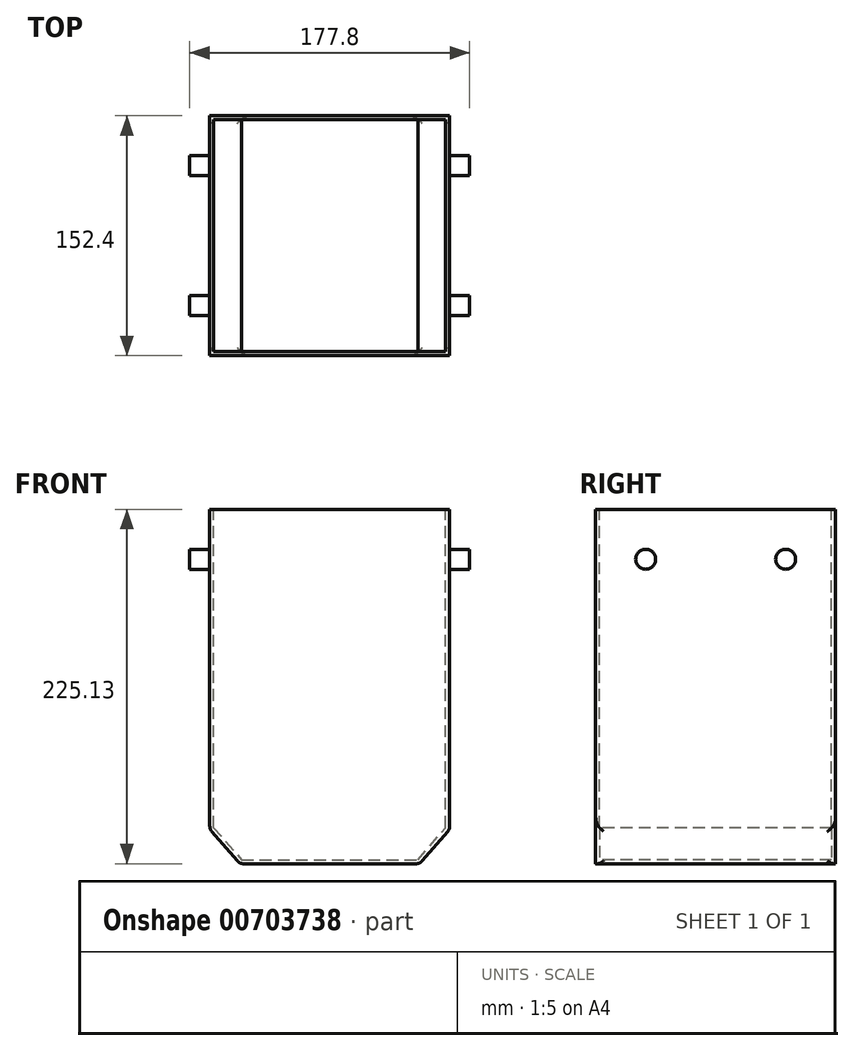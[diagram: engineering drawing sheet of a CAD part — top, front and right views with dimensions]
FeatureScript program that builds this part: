
annotation { "Feature Type Name" : "Feature", "Feature Type Description" : "" }
export const myFeature = defineFeature(function(context is Context, id is Id, definition is map)
    precondition{}
    {
        {
            var Q0;
            Q0=qCreatedBy(makeId("Front.planeOp"),FACE);
            var sketch = newSketch(context, id + "F0", { "sketchPlane" : qUnion([Q0])});
            skLineSegment(sketch, "E0.bottom", {"start": v(-76.2, -101.6) * mm, "end": v(76.2, -101.6) * mm});
            skLineSegment(sketch, "E0.top", {"start": v(-76.2, 101.6) * mm, "end": v(76.2, 101.6) * mm});
            skLineSegment(sketch, "E0.left", {"start": v(-76.2, -101.6) * mm, "end": v(-76.2, 101.6) * mm});
            skLineSegment(sketch, "E0.right", {"start": v(76.2, -101.6) * mm, "end": v(76.2, 101.6) * mm});
            skPoint(sketch, "E0.middle", {"position": v(0, 0) * mm});
            skLineSegment(sketch, "E1.bottom", {"start": v(-57.15, -123.53) * mm, "end": v(57.15, -123.53) * mm});
            skLineSegment(sketch, "E1.top", {"start": v(-57.15, -79.67) * mm, "end": v(57.15, -79.67) * mm});
            skLineSegment(sketch, "E1.left", {"start": v(-57.15, -123.53) * mm, "end": v(-57.15, -79.67) * mm});
            skLineSegment(sketch, "E1.right", {"start": v(57.15, -123.53) * mm, "end": v(57.15, -79.67) * mm});
            skPoint(sketch, "E1.middle", {"position": v(0, -101.6) * mm});
            skLineSegment(sketch, "E2", {"start": v(-76.2, -101.6) * mm, "end": v(-57.15, -123.53) * mm});
            skLineSegment(sketch, "E3", {"start": v(57.15, -123.53) * mm, "end": v(76.2, -101.6) * mm});
            skSolve(sketch);
        }
        {
            var Q0;
            {var subQ0=sQuery(id+"F0.wireOp",EDGE,"E2");Q0=makeQuery(id+"F0.imprint","IMPRINT",FACE,{"disambiguationData":[TD([[makeQuery(id+"F0.imprint","IMPRINT",EDGE,{"derivedFrom":subQ0}),1.0]])]});}
            var Q1;
            {var subQ0=sQuery(id+"F0.wireOp",EDGE,"E3");Q1=makeQuery(id+"F0.imprint","IMPRINT",FACE,{"disambiguationData":[TD([[makeQuery(id+"F0.imprint","IMPRINT",EDGE,{"derivedFrom":subQ0}),1.0]])]});}
            var Q2;
            Q2=makeQuery(id+"F0.imprint","IMPRINT",FACE,{"disambiguationData":[TD([[makeQuery(id+"F0.imprint","IMPRINT",EDGE,{"derivedFrom":sQuery(id+"F0.wireOp",EDGE,"E0.top")}),-1.0]])]});
            var Q3;
            {var subQ5=sQuery(id+"F0.wireOp",EDGE,"E1.top");Q3=makeQuery(id+"F0.imprint","IMPRINT",FACE,{"disambiguationData":[TD([[makeQuery(id+"F0.imprint","IMPRINT",EDGE,{"derivedFrom":subQ5}),-1.0]])]});}
            var Q4;
            {var subQ5=sQuery(id+"F0.wireOp",EDGE,"E1.bottom");Q4=makeQuery(id+"F0.imprint","IMPRINT",FACE,{"disambiguationData":[TD([[makeQuery(id+"F0.imprint","IMPRINT",EDGE,{"derivedFrom":subQ5}),1.0]])]});}
            var Q5;
            Q5 = qSketchRegion(id + "F0", true);
            extrude(context, id + "F1", {"entities" : qUnion([Q0, Q1, Q2, Q3, Q4, Q5]), "oppositeDirection" : true, "depth" : 76.2 * mm, "offsetDistance" : 25.4 * mm, "hasSecondDirection" : true, "secondDirectionOppositeDirection" : false, "secondDirectionDepth" : 76.2 * mm});
        }
        {
            var Q0;
            Q0=makeQuery(id+"F1.opExtrude","SWEPT_FACE",FACE,{"disambiguationData":[OSD([sQuery(id+"F0.wireOp",EDGE,"E0.top")])]});
            shell(context, id + "F2", {"entities" : qUnion([Q0]), "thickness" : 2.54 * mm});
        }
        {
            var Q0;
            Q0=makeQuery(id+"F1.opExtrude","SWEPT_FACE",FACE,{"disambiguationData":[OSD([sQuery(id+"F0.wireOp",EDGE,"E2")])]});
            var Q1;
            Q1=makeQuery(id+"F1.opExtrude","SWEPT_FACE",FACE,{"disambiguationData":[OSD([sQuery(id+"F0.wireOp",EDGE,"E3")])]});
            fillet(context, id + "F3", {"entities" : qUnion([Q0, Q1]), "radius" : 5.08 * mm, "tangentPropagation" : true, "allowEdgeOverflow" : false});
        }
        {
            var Q0;
            Q0=makeQuery(id+"F1.opExtrude","SWEPT_FACE",FACE,{"disambiguationData":[OSD([sQuery(id+"F0.wireOp",EDGE,"E0.left")])]});
            var sketch = newSketch(context, id + "F4", { "sketchPlane" : qUnion([Q0])});
            skCircle(sketch, "E4", {"center": v(-44.45, 69.85) * mm, "radius": 6.35 * mm});
            skCircle(sketch, "E5", {"center": v(44.45, 69.85) * mm, "radius": 6.35 * mm});
            skSolve(sketch);
        }
        {
            var Q0;
            Q0=makeQuery(id+"F4.imprint","IMPRINT",FACE,{"disambiguationData":[TD([[makeQuery(id+"F4.imprint","IMPRINT",EDGE,{"derivedFrom":sQuery(id+"F4.wireOp",EDGE,"E4")}),1.0]])]});
            var Q1;
            Q1=makeQuery(id+"F4.imprint","IMPRINT",FACE,{"disambiguationData":[TD([[makeQuery(id+"F4.imprint","IMPRINT",EDGE,{"derivedFrom":sQuery(id+"F4.wireOp",EDGE,"E5")}),1.0]])]});
            var Q2;
            Q2 = qSketchRegion(id + "F4", true);
            extrude(context, id + "F5", {"entities" : qUnion([Q0, Q1, Q2]), "operationType" : NewBodyOperationType.ADD, "depth" : 12.7 * mm, "offsetDistance" : 25.4 * mm});
        }
        {
            var Q0;
            Q0=makeQuery(id+"F1.opExtrude","SWEPT_FACE",FACE,{"disambiguationData":[OSD([sQuery(id+"F0.wireOp",EDGE,"E0.right")])]});
            var sketch = newSketch(context, id + "F6", { "sketchPlane" : qUnion([Q0])});
            skCircle(sketch, "E6", {"center": v(-44.45, 69.85) * mm, "radius": 6.35 * mm});
            skCircle(sketch, "E7", {"center": v(44.45, 69.85) * mm, "radius": 6.35 * mm});
            skSolve(sketch);
        }
        {
            var Q0;
            Q0 = qSketchRegion(id + "F6", true);
            var Q1;
            Q1=makeQuery(id+"F6.imprint","IMPRINT",FACE,{"disambiguationData":[TD([[makeQuery(id+"F6.imprint","IMPRINT",EDGE,{"derivedFrom":sQuery(id+"F6.wireOp",EDGE,"E7")}),1.0]])]});
            var Q2;
            Q2=makeQuery(id+"F6.imprint","IMPRINT",FACE,{"disambiguationData":[TD([[makeQuery(id+"F6.imprint","IMPRINT",EDGE,{"derivedFrom":sQuery(id+"F6.wireOp",EDGE,"E6")}),1.0]])]});
            extrude(context, id + "F7", {"entities" : qUnion([Q0, Q1, Q2]), "operationType" : NewBodyOperationType.ADD, "depth" : 12.7 * mm, "offsetDistance" : 25.4 * mm});
        }
    });
